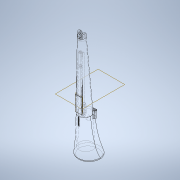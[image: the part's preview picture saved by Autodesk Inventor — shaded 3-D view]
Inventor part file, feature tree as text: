
AUTODESK INVENTOR PART (.ipt)
format: ipt  version: 2021 (Build 250183000, 183)  size: 909,824 bytes
history: native  units: mm
features: sketch x37, extrude x22, plane x17, fillet x4, hole x3, loft x2, revolve x2, other x1, thread x1
ambient origin geometry x8: Origin, YZ Plane, XZ Plane, XY Plane, X Axis, Y Axis, Z Axis, Center Point
bodies: Body1 (feature_tree)
feature tree (89):
  other  "Sólido1"
  plane  "Plano de trabajo1"
  plane  "Plano de trabajo2"
  plane  "Plano de trabajo4"
  plane  "Plano de trabajo5"
  plane  "Plano de trabajo6"
  sketch  "Boceto1"  dims[d1=250.0mm d2=0.0mm d3=-80.0mm d4=-110.0mm]
  sketch  "Boceto2"  dims[d5=-140.0mm d7=-0.0mm d8=2.0mm]
  sketch  "Boceto3"  dims[d9=140.0mm d10=250.0mm]
  sketch  "Boceto4"  dims[d11=24.0mm d22=0.0mm d23=90.0deg d24=0.0mm d25=90.0deg]
  sketch  "Boceto6"  dims[d44=45.0mm d49=29.11157mm]
  sketch  "Boceto7"  dims[d50=29.11157mm d53=29.11157mm]
  loft  "Solevación1"
  fillet  "Empalme2"  [1 undecoded]
  extrude  "Extrusión1"  TaperAngle=0.0deg  [1 undecoded]
  fillet  "Empalme5"  Radius=2.0mm
  plane  "Plano de trabajo7"
  extrude  "Extrusión2"  Depth=250.0mm
  plane  "Plano de trabajo8"
  plane  "Plano de trabajo9"
  loft  "Solevación9"
  plane  "Plano de trabajo10"
  extrude  "Extrusión3"  Depth=29.11157mm
  plane  "Plano de trabajo11"
  revolve  "Revolución1"  [1 undecoded]
  revolve  "Revolución2"  [1 undecoded]
  extrude  "Extrusión4"  Depth=22.5mm
  plane  "Plano de trabajo12"
  extrude  "Extrusión5"  Depth=22.5mm
  plane  "Plano de trabajo13"
  plane  "Plano de trabajo14"
  extrude  "Extrusión6"  Depth=42.747934mm
  extrude  "Extrusión7"  Depth=42.747934mm
  extrude  "Extrusión8"  Depth=13.0mm
  extrude  "Extrusión11"  Depth=7.75mm
  extrude  "Extrusión9"  Depth=7.75mm
  extrude  "Extrusión10"  Depth=16.0mm
  extrude  "Extrusión12"  Depth=12.0mm
  sketch  "Boceto30"  dims[d160=-19.75mm d161=0.0mm]
  extrude  "Extrusión13"  Depth=7.75mm
  extrude  "Extrusión14"  Depth=7.75mm
  extrude  "Extrusión15"  TaperAngle=0.0deg  [1 undecoded]
  hole  "Agujero1"  [1 undecoded]
  thread  "Rosca1"  [1 undecoded]
  extrude  "Extrusión16"  Depth=2.0mm
  plane  "Plano de trabajo16"
  extrude  "Extrusión17"  TaperAngle=0.0deg  [1 undecoded]
  extrude  "Extrusión18"  TaperAngle=0.0deg  [1 undecoded]
  plane  "Plano de trabajo17"
  sketch  "Boceto46"  dims[d182=0.25mm]
  hole  "Agujero2"  [1 undecoded]
  hole  "Agujero3"  [1 undecoded]
  plane  "Plano de trabajo19"
  sketch  "Boceto50"  dims[d185=2.0mm]
  sketch  "Boceto45"  dims[d181=0.75mm]
  fillet  "Empalme6"  Radius=30.0mm
  fillet  "Empalme7"  Radius=12.0mm
  sketch  "Boceto44"  dims[d180=0.75mm]
  sketch  "Boceto47"  dims[d183=1.0mm]
  sketch  "Boceto49"  dims[d184=0.25mm]
  extrude  "Extrusión22"  [1 undecoded]
  extrude  "Extrusión23"  Depth=0.75mm
  extrude  "Extrusión24"  Depth=2.5mm
  plane  "Plano de trabajo20"
  extrude  "Extrusión25"  Depth=17.453293mm
  sketch  "Boceto9"  dims[d59=29.11157mm d61=29.11157mm]
  sketch  "Boceto10"  dims[d65=22.5mm d66=32.5mm]
  sketch  "Boceto15"  dims[d67=22.5mm d90=44.747934mm]
  sketch  "Boceto16"  dims[d91=42.747934mm d93=42.747934mm]
  sketch  "Boceto17"  dims[d96=0.0mm d97=90.0deg d98=0.0mm d99=90.0deg d100=0.0mm d101=90.0deg d102=0.0mm d103=90.0deg d112=42.747934mm]
  sketch  "Boceto18"  dims[d115=5.0mm d120=13.0mm]
  sketch  "Boceto19"  dims[d121=6.5mm d124=7.75mm]
  sketch  "Boceto20"  dims[d125=7.75mm d126=7.75mm]
  sketch  "Boceto21"  dims[d127=7.75mm d130=16.0mm]
  sketch  "Boceto22"  dims[d131=0.0mm d132=12.0mm]
  sketch  "Boceto24"  dims[d133=12.0mm d134=7.75mm]
  sketch  "Boceto25"  dims[d135=6.5mm d136=7.75mm]
  sketch  "Boceto26"  dims[d137=15.0mm d138=0.0mm]
  sketch  "Boceto27"  dims[d146=-8.5mm d147=30.0mm d148=2.0mm]
  sketch  "Boceto28"  dims[d149=25.12mm d150=2.0mm]
  sketch  "Boceto29"  dims[d151=10.357mm d156=0.0mm d157=90.0deg d158=0.0mm d159=90.0deg]
  sketch  "Boceto31"  dims[d163=0.0mm d164=2.0mm]
  sketch  "Boceto36"  dims[d165=15.0mm d166=4.0mm d167=30.0mm d168=12.0mm]
  sketch  "Boceto37"  dims[d169=0.0mm d170=-7.25mm]
  sketch  "Boceto38"  dims[d171=4.5mm d172=0.75mm]
  sketch  "Boceto39"  dims[d173=2.5mm d174=1.0mm]
  sketch  "Boceto40"  dims[d176=11.0mm d177=17.453293mm]
  sketch  "Boceto41"  dims[d179=2.939597mm]
  sketch  "Boceto51"  dims[d187=1.0mm d189=3.0mm d190=2.0mm d191=2.0mm d192=0.25mm d193=0.25mm d194=90.0deg d196=4.381635mm d197=0.0mm d198=-48.35mm d199=12.0mm d200=20.0mm d201=9.0mm d202=9.0mm d203=2.0mm d204=201.65mm d205=0.0mm d206=0.5mm d207=0.25mm d208=-7.5mm d209=100.0mm d210=0.0mm d211=35.0mm d212=0.0mm d213=210.0mm d214=0.0mm d215=2.0mm d216=1.059493mm d217=6.5mm d218=1.059493mm d219=5.0mm d220=2.0mm d221=0.0mm d222=2.0mm d223=6.5mm d224=1.059493mm d225=5.0mm d226=4.85mm d227=2.0mm d228=0.0mm d229=6.0mm d230=10.0mm d231=3.0mm d232=11.0mm d233=10.5mm d235=30.0deg d236=4.75mm d237=0.0mm d238=-17.0mm d239=100.0mm d240=0.0mm d241=6.5mm d242=1.65mm d243=3.3mm d244=15.6mm d245=2.0mm d247=16.0mm d248=2.0mm d249=0.0mm d250=4.5mm d251=0.75mm d252=2.5mm d253=1.0mm d254=11.0mm d255=17.453293mm d256=2.939597mm d257=0.75mm d258=0.75mm d259=0.25mm d260=1.0mm d261=0.25mm d262=2.0mm d263=1.0mm d264=3.0mm d265=2.0mm d266=2.0mm d267=0.25mm d268=0.25mm d269=40.0mm d270=1.0mm d271=1.0mm d272=7.75mm d273=0.5mm d274=8.5mm d275=90.0deg d276=0.0mm d277=17.75mm d280=22.5mm d281=2.0mm d282=0.0mm d283=0.0mm d292=2.0mm d293=0.0mm d296=3.5mm d297=0.0mm d299=4.0mm d300=3.708mm d301=3.023mm d302=2.0mm d303=14.3117mm d304=16.0mm d305=0.0mm d306=16.0mm d307=0.0mm d314=6.0mm d315=19.2mm d316=6.0mm d317=19.2mm d318=13.0mm d320=6.0mm d321=19.2mm d322=13.0mm d323=6.0mm d324=19.2mm d325=13.0mm d326=7.0mm d332=10.0mm d333=0.0mm d335=-41.6mm d336=4.0mm d337=1.0mm d338=9.0mm d339=4.0mm d340=1.0mm d341=9.0mm d342=4.0mm d343=5.2mm d344=6.0mm d345=0.0mm d346=15.0mm d347=5.0mm d349=5.0mm d351=0.0mm d352=45.0mm d354=10.0mm d355=10.0mm d356=0.0mm d357=15.0mm d358=0.0mm d359=2.0mm d363=50.4125mm d376=14.059493mm d377=2.0mm d378=0.0mm d379=2.0mm d380=11.25mm d381=90.0mm d382=290.0mm d383=14.059493mm d384=100.825mm d390=30.940507mm d391=2.0mm d392=100.825mm d393=14.790546mm d394=2.0mm d395=3.0mm d396=6.0mm d397=4.0mm d398=4.0mm d399=4.0mm d400=8.128453mm d401=12.0mm d402=4.45mm d403=2.5mm d404=1.65mm d405=1.65mm d406=1.0mm d407=2.0mm d408=2.0mm d409=0.0mm d411=50.4125mm d412=6.0mm d418=13.059493mm d419=6.5mm d420=6.5mm d421=50.4125mm d422=126.03125mm d423=0.0mm d424=15.0mm d425=5.0mm d426=5.0mm d427=0.0mm d428=45.0mm d429=10.0mm d430=2.0mm d431=4.0mm d432=6.0mm d433=8.0mm d434=2.0mm d435=90.0deg d436=20.0mm d437=0.0mm d438=4.0mm d439=6.0mm d440=8.0mm d441=2.0mm d442=90.0deg d443=20.0mm d444=0.0mm d446=10.0mm d447=3.0mm d448=11.5mm d450=9.0mm d451=9.0mm d452=90.0mm d453=750.0mm d454=22.5mm d455=43.0mm d456=44.0mm d457=14.059493mm d458=11.25mm d461=22.5mm d462=43.0mm d463=7.059493mm d464=3.0mm d465=6.0mm d466=3.0mm d467=6.0mm d468=45.0mm d469=65.5mm d470=19.749mm d471=24.0mm d472=12.0mm d473=1.0mm d474=1.5mm d475=2.0mm d476=1.5mm d477=2.0mm d478=55.5mm d479=0.0mm d480=55.5mm d481=0.0mm d482=51.5mm d483=0.0mm d484=37.0mm d485=0.0mm d486=-2.5mm d487=32.279486mm d488=1.6mm d489=60.0deg d490=45.0deg d491=12.0mm d492=1.6mm d493=0.0mm]
note: 12 required parameter values undecoded (feature->parameter linkage not recoverable at this tier; creation-order binding heuristic only, values carry confidence <= 0.55)